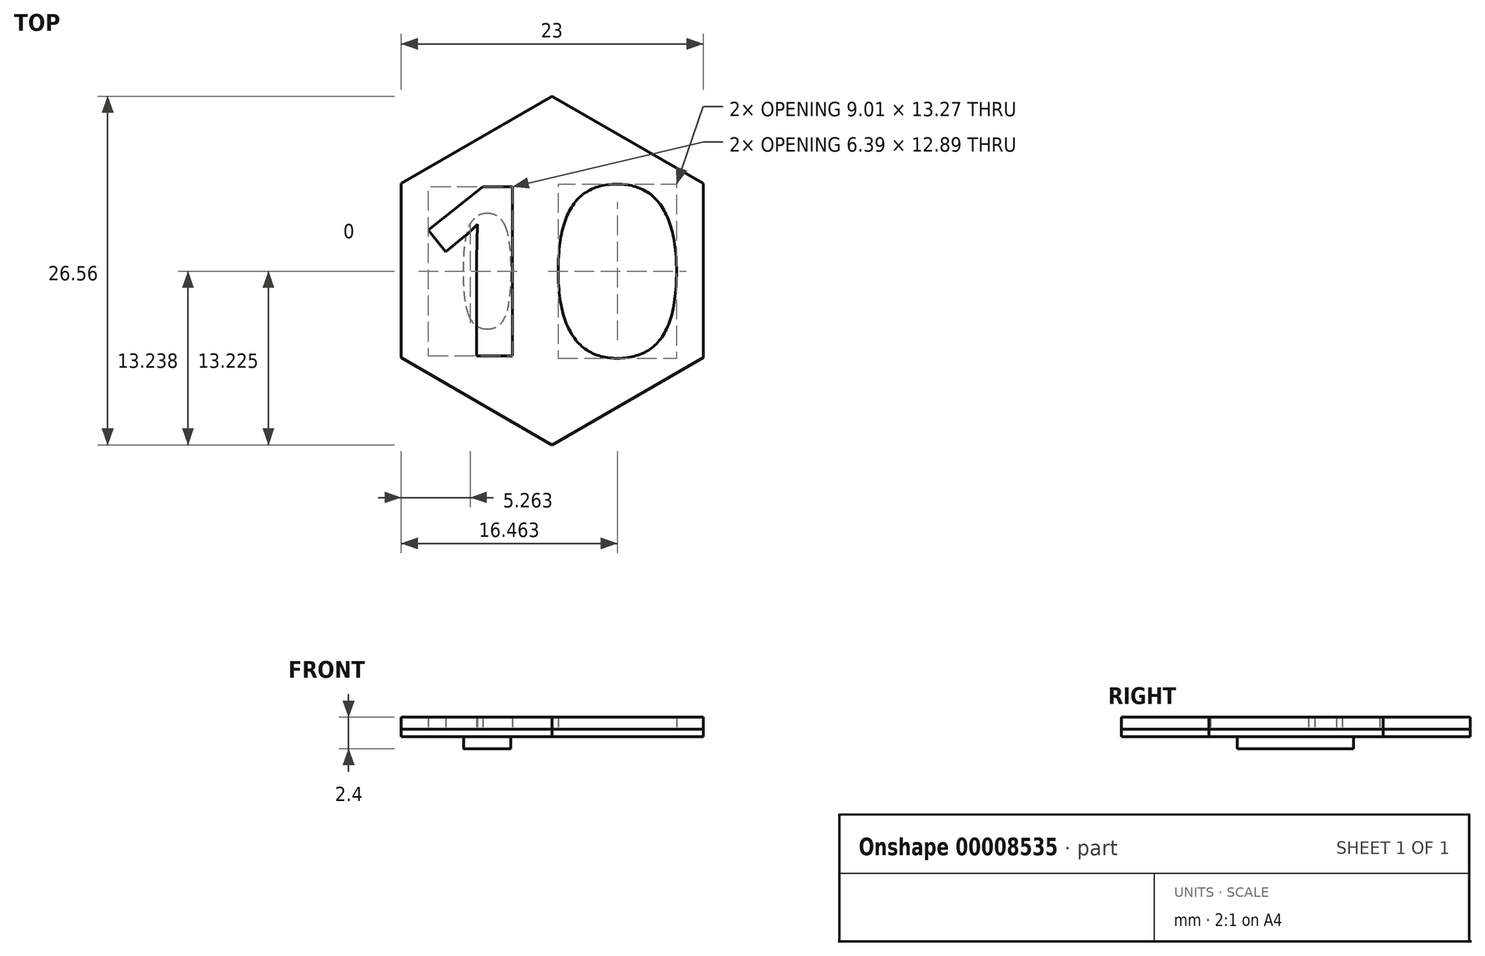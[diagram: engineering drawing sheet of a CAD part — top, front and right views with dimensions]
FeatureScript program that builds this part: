
annotation { "Feature Type Name" : "Feature", "Feature Type Description" : "" }
export const myFeature = defineFeature(function(context is Context, id is Id, definition is map)
    precondition{}
    {
        {
            var Q0;
            Q0=qCreatedBy(makeId("Top.planeOp"),FACE);
            var sketch = newSketch(context, id + "F0", { "sketchPlane" : qUnion([Q0])});
            skText(sketch, "E0", { "text": "10", "fontName": "OpenSans-Bold.ttf"});
            skLineSegment(sketch, "E1", {"start": v(-51.5, -6.5) * mm, "end": v(3.11, -6.5) * mm, "construction": true});
            skLineSegment(sketch, "E2", {"start": v(0, 0) * mm, "end": v(0, 15.36) * mm, "construction": true});
            skCircle(sketch, "E3.cCircle", {"center": v(0, 0) * mm, "radius": 11.5 * mm, "construction": true});
            skLineSegment(sketch, "E3.0", {"start": v(-11.5, -6.64) * mm, "end": v(-11.5, 6.64) * mm});
            skLineSegment(sketch, "E3.1", {"start": v(-11.5, 6.64) * mm, "end": v(0, 13.28) * mm});
            skLineSegment(sketch, "E3.2", {"start": v(0, 13.28) * mm, "end": v(11.5, 6.64) * mm});
            skLineSegment(sketch, "E3.3", {"start": v(11.5, 6.64) * mm, "end": v(11.5, -6.64) * mm});
            skLineSegment(sketch, "E3.4", {"start": v(11.5, -6.64) * mm, "end": v(0, -13.28) * mm});
            skLineSegment(sketch, "E3.5", {"start": v(0, -13.28) * mm, "end": v(-11.5, -6.64) * mm});
            skPoint(sketch, "E3.0.midPoint", {"position": v(-11.5, 0) * mm});
            const initialGuessF0  = {"E0": [-0.0105, -0.0065, 1, 0, 0.013]};
            skSetInitialGuess(sketch, initialGuessF0);
            skSolve(sketch);
        }
        {
            var Q0;
            Q0=makeQuery(id+"F0.imprint","IMPRINT",FACE,{"disambiguationData":[TD([[makeQuery(id+"F0.imprint","IMPRINT",EDGE,{"derivedFrom":sQuery(id+"F0.wireOp",EDGE,"E0.sketch_text.stroke-0")}),1.0]])]});
            var Q1;
            Q1=makeQuery(id+"F0.imprint","IMPRINT",FACE,{"disambiguationData":[TD([[makeQuery(id+"F0.imprint","IMPRINT",EDGE,{"derivedFrom":sQuery(id+"F0.wireOp",EDGE,"E0.sketch_text.stroke-18")}),1.0]])]});
            extrude(context, id + "F1", {"entities" : qUnion([Q0, Q1]), "depth" : 0.9 * mm, "offsetDistance" : 25 * mm});
        }
        {
            var Q0;
            Q0=makeQuery(id+"F0.imprint","IMPRINT",FACE,{"disambiguationData":[TD([[makeQuery(id+"F0.imprint","IMPRINT",EDGE,{"derivedFrom":sQuery(id+"F0.wireOp",EDGE,"E0.sketch_text.stroke-0")}),1.0]])]});
            var Q1;
            Q1=makeQuery(id+"F0.imprint","IMPRINT",FACE,{"disambiguationData":[TD([[makeQuery(id+"F0.imprint","IMPRINT",EDGE,{"derivedFrom":sQuery(id+"F0.wireOp",EDGE,"E0.sketch_text.stroke-0")}),-1.0]])]});
            var Q2;
            Q2=makeQuery(id+"F0.imprint","IMPRINT",FACE,{"disambiguationData":[TD([[makeQuery(id+"F0.imprint","IMPRINT",EDGE,{"derivedFrom":sQuery(id+"F0.wireOp",EDGE,"E0.sketch_text.stroke-10")}),-1.0]])]});
            var Q3;
            Q3=makeQuery(id+"F0.imprint","IMPRINT",FACE,{"disambiguationData":[TD([[makeQuery(id+"F0.imprint","IMPRINT",EDGE,{"derivedFrom":sQuery(id+"F0.wireOp",EDGE,"E0.sketch_text.stroke-18")}),1.0]])]});
            extrude(context, id + "F2", {"entities" : qUnion([Q0, Q1, Q2, Q3]), "oppositeDirection" : true, "depth" : 0.6 * mm, "offsetDistance" : 25 * mm});
        }
        {
            var Q0;
            Q0=makeQuery(id+"F1.opExtrude","SWEPT_BODY",BODY,{"disambiguationData":[OSD([sQuery(id+"F0.wireOp",EDGE,"lMo7d26n-KwDa-lOEM-g7Ql-aikgDYs5bSy0"),sQuery(id+"F0.wireOp",EDGE,"E0.sketch_text.stroke-0"),sQuery(id+"F0.wireOp",EDGE,"E0.sketch_text.stroke-1"),sQuery(id+"F0.wireOp",EDGE,"E0.sketch_text.stroke-2"),sQuery(id+"F0.wireOp",EDGE,"E0.sketch_text.stroke-3"),sQuery(id+"F0.wireOp",EDGE,"E0.sketch_text.stroke-4"),sQuery(id+"F0.wireOp",EDGE,"E0.sketch_text.stroke-5"),sQuery(id+"F0.wireOp",EDGE,"E0.sketch_text.stroke-6"),sQuery(id+"F0.wireOp",EDGE,"E0.sketch_text.stroke-7"),sQuery(id+"F0.wireOp",EDGE,"E0.sketch_text.stroke-8"),sQuery(id+"F0.wireOp",EDGE,"E0.sketch_text.stroke-9"),sQuery(id+"F0.wireOp",EDGE,"E0.sketch_text.stroke-10"),sQuery(id+"F0.wireOp",EDGE,"E0.sketch_text.stroke-11"),sQuery(id+"F0.wireOp",EDGE,"E0.sketch_text.stroke-12"),sQuery(id+"F0.wireOp",EDGE,"E0.sketch_text.stroke-13"),sQuery(id+"F0.wireOp",EDGE,"E0.sketch_text.stroke-14"),sQuery(id+"F0.wireOp",EDGE,"E0.sketch_text.stroke-15"),sQuery(id+"F0.wireOp",EDGE,"E0.sketch_text.stroke-16"),sQuery(id+"F0.wireOp",EDGE,"E0.sketch_text.stroke-17"),sQuery(id+"F0.wireOp",EDGE,"E0.sketch_text.stroke-18"),sQuery(id+"F0.wireOp",EDGE,"E0.sketch_text.stroke-19"),sQuery(id+"F0.wireOp",EDGE,"E0.sketch_text.stroke-20"),sQuery(id+"F0.wireOp",EDGE,"E0.sketch_text.stroke-21"),sQuery(id+"F0.wireOp",EDGE,"E0.sketch_text.stroke-22"),sQuery(id+"F0.wireOp",EDGE,"E0.sketch_text.stroke-23")])]});
            var Q1;
            Q1=makeQuery(id+"F1.opExtrude","SWEPT_BODY",BODY,{"disambiguationData":[OSD([sQuery(id+"F0.wireOp",EDGE,"E0.sketch_text.stroke-18"),sQuery(id+"F0.wireOp",EDGE,"E0.sketch_text.stroke-19"),sQuery(id+"F0.wireOp",EDGE,"E0.sketch_text.stroke-20"),sQuery(id+"F0.wireOp",EDGE,"E0.sketch_text.stroke-21"),sQuery(id+"F0.wireOp",EDGE,"E0.sketch_text.stroke-22"),sQuery(id+"F0.wireOp",EDGE,"E0.sketch_text.stroke-23"),sQuery(id+"F0.wireOp",EDGE,"E0.sketch_text.stroke-24"),sQuery(id+"F0.wireOp",EDGE,"E0.sketch_text.stroke-25")])]});
            transform(context, id + "F3", {"entities" : qUnion([Q0, Q1]), "transformType" : TransformType.TRANSLATION_3D, "dx" : 0 * mm, "dy" : 0 * mm, "dz" : 0 * mm, "makeCopy" : true});
        }
        {
            var Q0;
            Q0=makeQuery(id+"F3.opPattern","COPY",BODY,{"derivedFrom":makeQuery(id+"F1.opExtrude","SWEPT_BODY",BODY,{"disambiguationData":[OSD([sQuery(id+"F0.wireOp",EDGE,"lMo7d26n-KwDa-lOEM-g7Ql-aikgDYs5bSy0"),sQuery(id+"F0.wireOp",EDGE,"E0.sketch_text.stroke-0"),sQuery(id+"F0.wireOp",EDGE,"E0.sketch_text.stroke-1"),sQuery(id+"F0.wireOp",EDGE,"E0.sketch_text.stroke-2"),sQuery(id+"F0.wireOp",EDGE,"E0.sketch_text.stroke-3"),sQuery(id+"F0.wireOp",EDGE,"E0.sketch_text.stroke-4"),sQuery(id+"F0.wireOp",EDGE,"E0.sketch_text.stroke-5"),sQuery(id+"F0.wireOp",EDGE,"E0.sketch_text.stroke-6"),sQuery(id+"F0.wireOp",EDGE,"E0.sketch_text.stroke-7"),sQuery(id+"F0.wireOp",EDGE,"E0.sketch_text.stroke-8"),sQuery(id+"F0.wireOp",EDGE,"E0.sketch_text.stroke-9"),sQuery(id+"F0.wireOp",EDGE,"E0.sketch_text.stroke-10"),sQuery(id+"F0.wireOp",EDGE,"E0.sketch_text.stroke-11"),sQuery(id+"F0.wireOp",EDGE,"E0.sketch_text.stroke-12"),sQuery(id+"F0.wireOp",EDGE,"E0.sketch_text.stroke-13"),sQuery(id+"F0.wireOp",EDGE,"E0.sketch_text.stroke-14"),sQuery(id+"F0.wireOp",EDGE,"E0.sketch_text.stroke-15"),sQuery(id+"F0.wireOp",EDGE,"E0.sketch_text.stroke-16"),sQuery(id+"F0.wireOp",EDGE,"E0.sketch_text.stroke-17"),sQuery(id+"F0.wireOp",EDGE,"E0.sketch_text.stroke-18"),sQuery(id+"F0.wireOp",EDGE,"E0.sketch_text.stroke-19"),sQuery(id+"F0.wireOp",EDGE,"E0.sketch_text.stroke-20"),sQuery(id+"F0.wireOp",EDGE,"E0.sketch_text.stroke-21"),sQuery(id+"F0.wireOp",EDGE,"E0.sketch_text.stroke-22"),sQuery(id+"F0.wireOp",EDGE,"E0.sketch_text.stroke-23")])]}),"instanceName":"1"});
            var Q1;
            Q1=makeQuery(id+"F1.opExtrude","SWEPT_BODY",BODY,{"disambiguationData":[OSD([sQuery(id+"F0.wireOp",EDGE,"E0.sketch_text.stroke-18"),sQuery(id+"F0.wireOp",EDGE,"E0.sketch_text.stroke-19"),sQuery(id+"F0.wireOp",EDGE,"E0.sketch_text.stroke-20"),sQuery(id+"F0.wireOp",EDGE,"E0.sketch_text.stroke-21"),sQuery(id+"F0.wireOp",EDGE,"E0.sketch_text.stroke-22"),sQuery(id+"F0.wireOp",EDGE,"E0.sketch_text.stroke-23"),sQuery(id+"F0.wireOp",EDGE,"E0.sketch_text.stroke-24"),sQuery(id+"F0.wireOp",EDGE,"E0.sketch_text.stroke-25")])]});
            var Q2;
            Q2=sQuery(id+"F0.wireOp",EDGE,"E2");
            transform(context, id + "F4", {"entities" : qUnion([Q0, Q1]), "transformType" : TransformType.ROTATION, "transformAxis" : qUnion([Q2]), "angle" : 180 * degree, "makeCopy" : false});
        }
        {
            var Q0;
            Q0=makeQuery(id+"F3.opPattern","COPY",BODY,{"derivedFrom":makeQuery(id+"F1.opExtrude","SWEPT_BODY",BODY,{"disambiguationData":[OSD([sQuery(id+"F0.wireOp",EDGE,"lMo7d26n-KwDa-lOEM-g7Ql-aikgDYs5bSy0"),sQuery(id+"F0.wireOp",EDGE,"E0.sketch_text.stroke-0"),sQuery(id+"F0.wireOp",EDGE,"E0.sketch_text.stroke-1"),sQuery(id+"F0.wireOp",EDGE,"E0.sketch_text.stroke-2"),sQuery(id+"F0.wireOp",EDGE,"E0.sketch_text.stroke-3"),sQuery(id+"F0.wireOp",EDGE,"E0.sketch_text.stroke-4"),sQuery(id+"F0.wireOp",EDGE,"E0.sketch_text.stroke-5"),sQuery(id+"F0.wireOp",EDGE,"E0.sketch_text.stroke-6"),sQuery(id+"F0.wireOp",EDGE,"E0.sketch_text.stroke-7"),sQuery(id+"F0.wireOp",EDGE,"E0.sketch_text.stroke-8"),sQuery(id+"F0.wireOp",EDGE,"E0.sketch_text.stroke-9"),sQuery(id+"F0.wireOp",EDGE,"E0.sketch_text.stroke-10"),sQuery(id+"F0.wireOp",EDGE,"E0.sketch_text.stroke-11"),sQuery(id+"F0.wireOp",EDGE,"E0.sketch_text.stroke-12"),sQuery(id+"F0.wireOp",EDGE,"E0.sketch_text.stroke-13"),sQuery(id+"F0.wireOp",EDGE,"E0.sketch_text.stroke-14"),sQuery(id+"F0.wireOp",EDGE,"E0.sketch_text.stroke-15"),sQuery(id+"F0.wireOp",EDGE,"E0.sketch_text.stroke-16"),sQuery(id+"F0.wireOp",EDGE,"E0.sketch_text.stroke-17"),sQuery(id+"F0.wireOp",EDGE,"E0.sketch_text.stroke-18"),sQuery(id+"F0.wireOp",EDGE,"E0.sketch_text.stroke-19"),sQuery(id+"F0.wireOp",EDGE,"E0.sketch_text.stroke-20"),sQuery(id+"F0.wireOp",EDGE,"E0.sketch_text.stroke-21"),sQuery(id+"F0.wireOp",EDGE,"E0.sketch_text.stroke-22"),sQuery(id+"F0.wireOp",EDGE,"E0.sketch_text.stroke-23")])]}),"instanceName":"1"});
            var Q1;
            Q1=makeQuery(id+"F1.opExtrude","SWEPT_BODY",BODY,{"disambiguationData":[OSD([sQuery(id+"F0.wireOp",EDGE,"E0.sketch_text.stroke-18"),sQuery(id+"F0.wireOp",EDGE,"E0.sketch_text.stroke-19"),sQuery(id+"F0.wireOp",EDGE,"E0.sketch_text.stroke-20"),sQuery(id+"F0.wireOp",EDGE,"E0.sketch_text.stroke-21"),sQuery(id+"F0.wireOp",EDGE,"E0.sketch_text.stroke-22"),sQuery(id+"F0.wireOp",EDGE,"E0.sketch_text.stroke-23"),sQuery(id+"F0.wireOp",EDGE,"E0.sketch_text.stroke-24"),sQuery(id+"F0.wireOp",EDGE,"E0.sketch_text.stroke-25")])]});
            transform(context, id + "F5", {"entities" : qUnion([Q0, Q1]), "transformType" : TransformType.TRANSLATION_3D, "dx" : 0 * mm, "dy" : 0 * mm, "dz" : -0.6 * mm, "makeCopy" : false});
        }
    });
